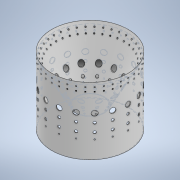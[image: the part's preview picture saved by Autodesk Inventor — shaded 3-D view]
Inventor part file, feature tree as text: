
AUTODESK INVENTOR PART (.ipt)
format: ipt  version: 2021.2 (Build 252289000, 289)  size: 1,136,128 bytes
history: native  units: in
note: dims shown in document units (in); Inventor stores cm internally (conversion verified against a paired STEP export)
features: sketch x5, extrude x4, pattern_circular x4, plane x2, revolve x1
ambient origin geometry x8: Origin, YZ Plane, XZ Plane, XY Plane, X Axis, Y Axis, Z Axis, Center Point
bodies: Solid1 (feature_tree)
feature tree (16):
  revolve  "Revolution1"  [1 undecoded]
  plane  "Work Plane1"
  extrude  "Extrusion1"  Depth=2.5in
  pattern_circular  "Circular Pattern1"  [2 undecoded]
  extrude  "Extrusion2"  Depth=0.0625in
  pattern_circular  "Circular Pattern2"  [2 undecoded]
  extrude  "Extrusion3"  Depth=0.0625in
  pattern_circular  "Circular Pattern3"  [2 undecoded]
  plane  "Work Plane2"
  extrude  "Extrusion4"  Depth=0.0625in
  pattern_circular  "Circular Pattern4"  [2 undecoded]
  sketch  "Sketch1"  dims[d0=1.7in d1=0.375in]
  sketch  "Sketch2"  dims[d2=0.7in d3=2.5in]
  sketch  "Sketch3"  dims[d4=1.0in]
  sketch  "Sketch4"  dims[d5=0.75in]
  sketch  "Sketch6"  dims[d6=0.875in d7=0.0in d9=1.85in d10=2.0in d11=0.25in d12=0.0in d14=0.1919in d15=0.1918in d17=0.0in d18=0.0312in d19=0.0in d20=90.0deg d21=2.0in d22=0.0625in d23=0.2in d30=1.0in d31=0.0in d32=14.1732in d33=360.0deg d35=0.0625in d36=0.4in d37=0.0in d38=0.25in d39=1.3in d40=1.5in d41=0.0in d42=4.7244in d43=360.0deg d45=0.125in d46=1.7in d47=1.5in d48=0.0in d49=4.7244in d50=360.0deg d52=-2.0in d53=0.5in d54=0.0in d55=7.0866in d56=360.0deg d58=0.0625in d59=0.2in d60=0.125in d61=2.1in d62=0.0625in d63=0.2in d64=0.0625in d65=0.3in d70=0.693in d71=0.6577in]
note: 9 required parameter values undecoded (feature->parameter linkage not recoverable at this tier; creation-order binding heuristic only, values carry confidence <= 0.55)